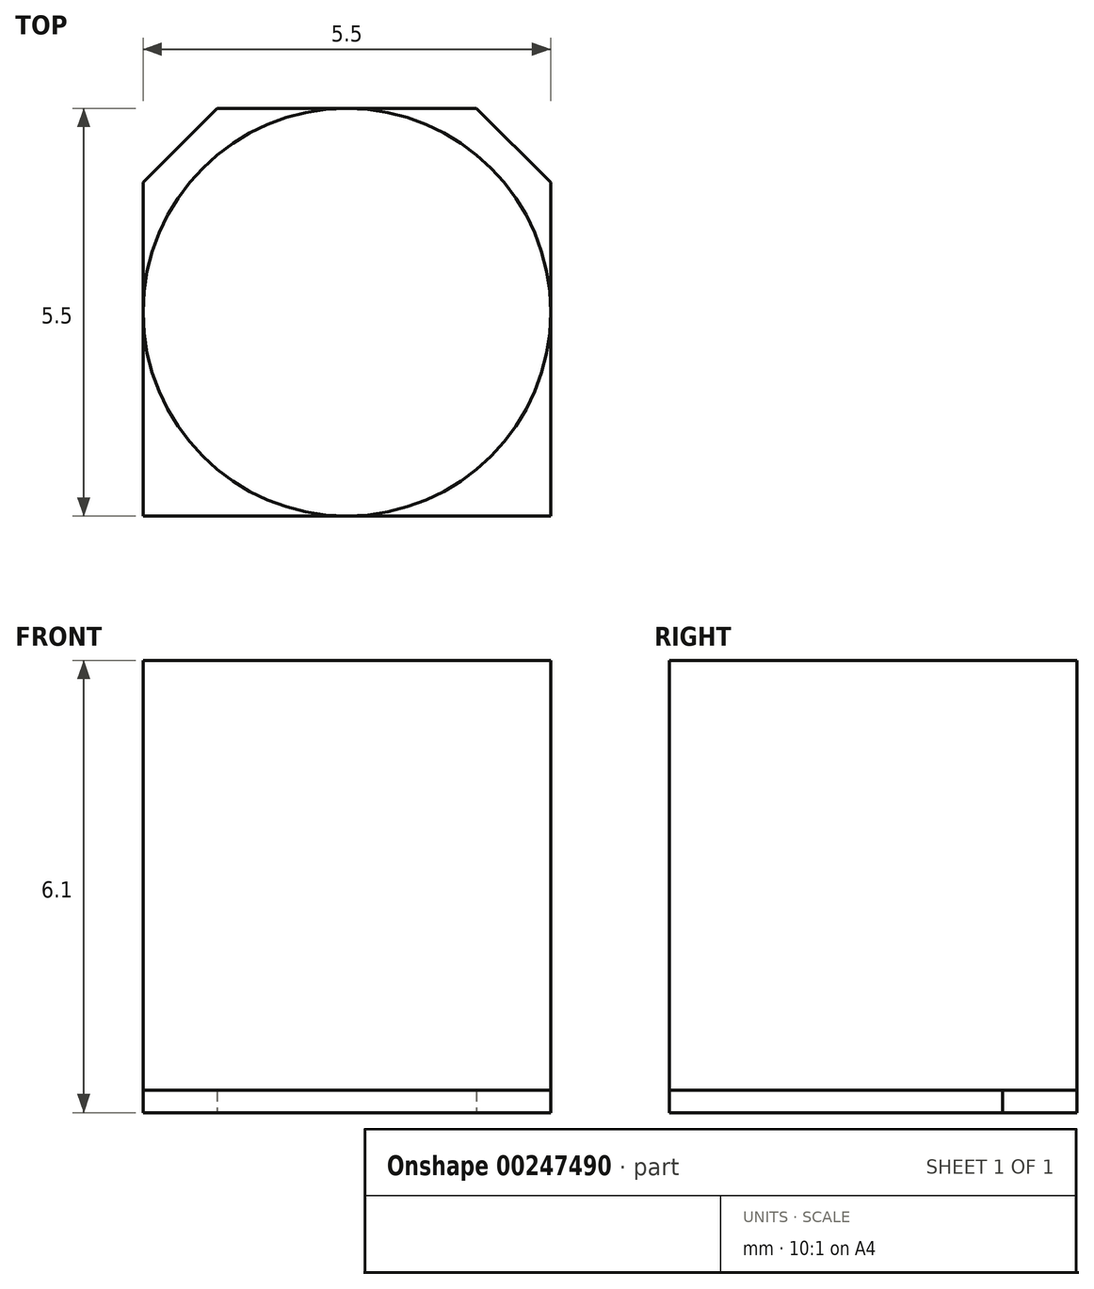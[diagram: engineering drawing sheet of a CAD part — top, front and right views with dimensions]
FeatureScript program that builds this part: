
annotation { "Feature Type Name" : "Feature", "Feature Type Description" : "" }
export const myFeature = defineFeature(function(context is Context, id is Id, definition is map)
    precondition{}
    {
        {
            var Q0;
            Q0=qCreatedBy(makeId("Top.planeOp"),FACE);
            var sketch = newSketch(context, id + "F0", { "sketchPlane" : qUnion([Q0])});
            skLineSegment(sketch, "E0.rect.bottom", {"start": v(2.75, -2.75) * mm, "end": v(-2.75, -2.75) * mm});
            skLineSegment(sketch, "E0.rect.top", {"start": v(1.75, 2.75) * mm, "end": v(-1.75, 2.75) * mm});
            skLineSegment(sketch, "E0.rect.left", {"start": v(2.75, -2.75) * mm, "end": v(2.75, 1.75) * mm});
            skLineSegment(sketch, "E0.rect.right", {"start": v(-2.75, -2.75) * mm, "end": v(-2.75, 1.75) * mm});
            skPoint(sketch, "E0.rect.middle", {"position": v(0, 0) * mm});
            skLineSegment(sketch, "E1", {"start": v(-2.75, 1.75) * mm, "end": v(-1.75, 2.75) * mm});
            skLineSegment(sketch, "E2", {"start": v(2.75, 1.75) * mm, "end": v(1.75, 2.75) * mm});
            skSolve(sketch);
        }
        {
            var Q0;
            Q0=makeQuery(id+"F0.imprint","IMPRINT",FACE,{"disambiguationData":[TD([[makeQuery(id+"F0.imprint","IMPRINT",EDGE,{"derivedFrom":sQuery(id+"F0.wireOp",EDGE,"E0.rect.bottom")}),-1.0]])]});
            extrude(context, id + "F1", {"entities" : qUnion([Q0]), "depth" : 0.3 * mm});
        }
        {
            var Q0;
            Q0=qCreatedBy(makeId("Top.planeOp"),FACE);
            var sketch = newSketch(context, id + "F2", { "sketchPlane" : qUnion([Q0])});
            skCircle(sketch, "E3", {"center": v(0, 0) * mm, "radius": 2.75 * mm});
            skSolve(sketch);
        }
        {
            var Q0;
            Q0=qSketchRegion(id+"F2",true);
            extrude(context, id + "F3", {"entities" : qUnion([Q0]), "operationType" : NewBodyOperationType.ADD, "depth" : 6.1 * mm});
        }
    });
